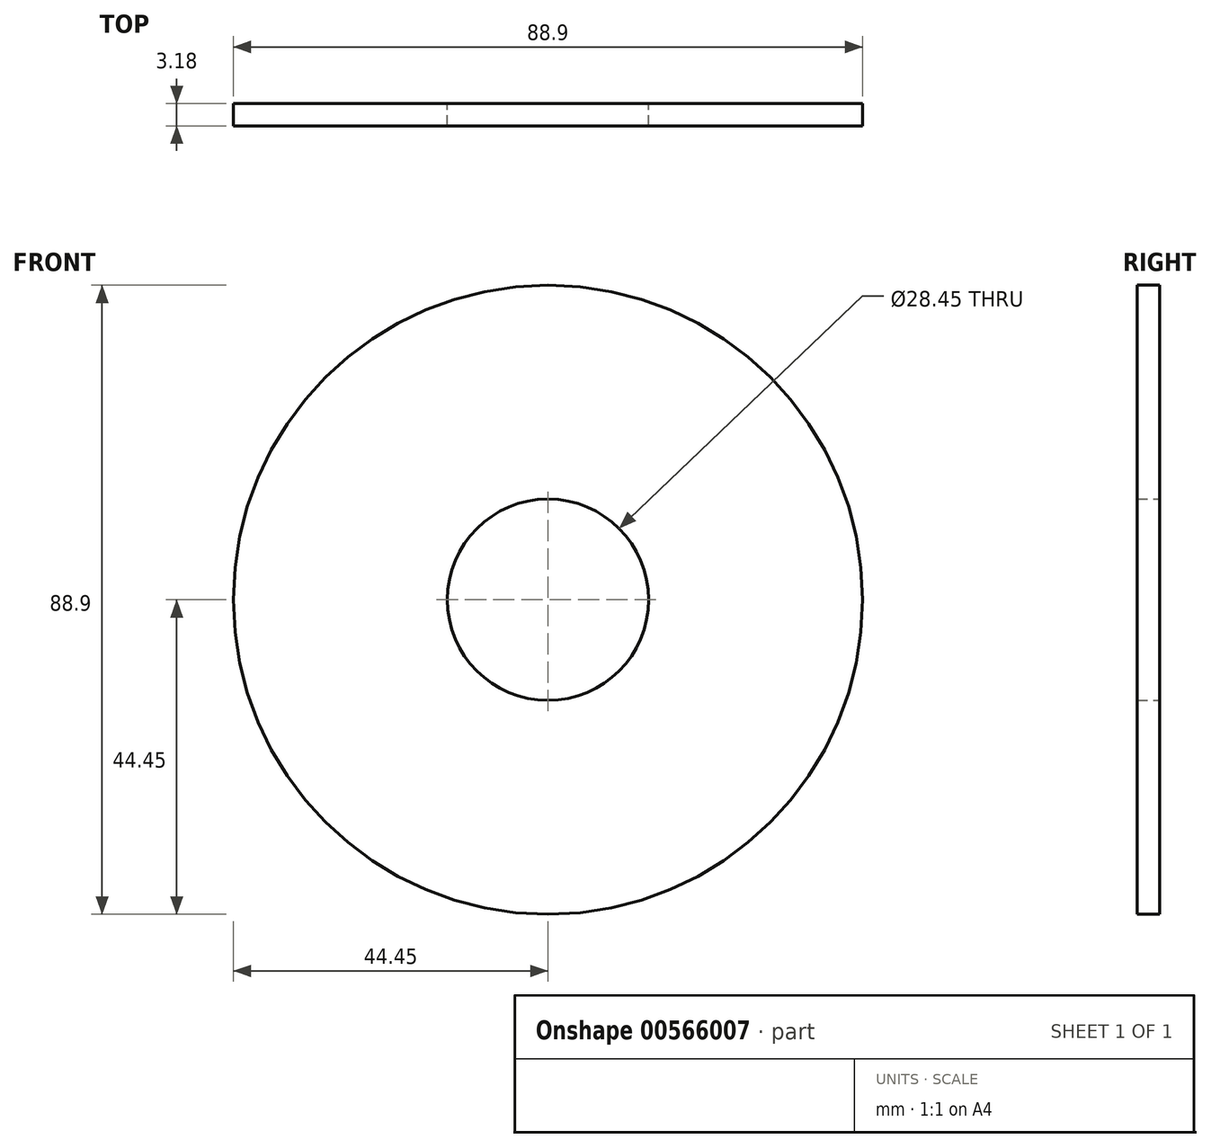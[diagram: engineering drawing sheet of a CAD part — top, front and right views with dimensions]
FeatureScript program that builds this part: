
annotation { "Feature Type Name" : "Feature", "Feature Type Description" : "" }
export const myFeature = defineFeature(function(context is Context, id is Id, definition is map)
    precondition{}
    {
        {
            var Q0;
            Q0=qCreatedBy(makeId("Front.planeOp"),FACE);
            var sketch = newSketch(context, id + "F0", { "sketchPlane" : qUnion([Q0])});
            skCircle(sketch, "E0", {"center": v(0, 0) * mm, "radius": 44.45 * mm});
            skCircle(sketch, "E1", {"center": v(0, 0) * mm, "radius": 14.22 * mm});
            skSolve(sketch);
        }
        {
            var Q0;
            Q0=makeQuery(id+"F0.imprint","IMPRINT",FACE,{"disambiguationData":[TD([[makeQuery(id+"F0.imprint","IMPRINT",EDGE,{"derivedFrom":sQuery(id+"F0.wireOp",EDGE,"E0")}),1.0]])]});
            extrude(context, id + "F1", {"entities" : qUnion([Q0]), "depth" : 3.17 * mm, "offsetDistance" : 25.4 * mm});
        }
    });
